annotation { "Feature Type Name" : "Feature", "Feature Type Description" : "" }
export const myFeature = defineFeature(function(context is Context, id is Id, definition is map)
    precondition{}
    {
        {
            var Q0;
            Q0=qCreatedBy(makeId("Top.planeOp"),FACE);
            var sketch = newSketch(context, id + "F0", { "sketchPlane" : qUnion([Q0])});
            skLineSegment(sketch, "E0.bottom", {"start": v(350, 500) * mm, "end": v(-1900, 500) * mm});
            skLineSegment(sketch, "E0.top", {"start": v(350, -500) * mm, "end": v(-1900, -500) * mm});
            skLineSegment(sketch, "E0.left", {"start": v(350, 500) * mm, "end": v(350, -500) * mm});
            skLineSegment(sketch, "E0.right", {"start": v(-1900, 500) * mm, "end": v(-1900, -500) * mm});
            skLineSegment(sketch, "E1.bottom", {"start": v(-1900, 223.65) * mm, "end": v(-4600, 223.65) * mm});
            skLineSegment(sketch, "E1.top", {"start": v(-1900, -223.65) * mm, "end": v(-4600, -223.65) * mm});
            skPoint(sketch, "E1.middle", {"position": v(-1900, 0) * mm});
            skLineSegment(sketch, "E2", {"start": v(-4600, 223.65) * mm, "end": v(-4600, -223.65) * mm});
            skLineSegment(sketch, "E3", {"start": v(-4100, 223.65) * mm, "end": v(-4100, -223.65) * mm});
            skText(sketch, "E4", { "text": "4A", "fontName": "OpenSans-Regular.ttf"});
            skText(sketch, "E5", { "text": "Working Area", "fontName": "OpenSans-Regular.ttf"});
            const initialGuessF0  = {"E4": [-1.64332, -0.3289, 1, 0, 0.6196], "E5": [-4.11386, -0.11617, 1, 0, 0.25472]};
            skSetInitialGuess(sketch, initialGuessF0);
            skSolve(sketch);
        }
        {
            var Q0;
            {var subQ5=sQuery(id+"F0.wireOp",EDGE,"E3");Q0=makeQuery(id+"F0.imprint","IMPRINT",FACE,{"disambiguationData":[TD([[makeQuery(id+"F0.imprint","IMPRINT",EDGE,{"derivedFrom":subQ5}),1.0]])]});}
            extrude(context, id + "F1", {"entities" : qUnion([Q0]), "depth" : 800 * mm});
        }
        {
            var Q0;
            {var subQ1=sQuery(id+"F0.wireOp",EDGE,"E0.bottom");Q0=makeQuery(id+"F0.imprint","IMPRINT",FACE,{"disambiguationData":[TD([[makeQuery(id+"F0.imprint","IMPRINT",EDGE,{"derivedFrom":subQ1}),1.0]])]});}
            extrude(context, id + "F2", {"entities" : qUnion([Q0]), "depth" : 800 * mm});
        }
        {
            var Q0;
            {var subQ0=sQuery(id+"F0.wireOp",EDGE,"E2");Q0=makeQuery(id+"F0.imprint","IMPRINT",FACE,{"disambiguationData":[TD([[makeQuery(id+"F0.imprint","IMPRINT",EDGE,{"derivedFrom":subQ0}),1.0]])]});}
            extrude(context, id + "F3", {"entities" : qUnion([Q0]), "depth" : 800 * mm});
        }
    });